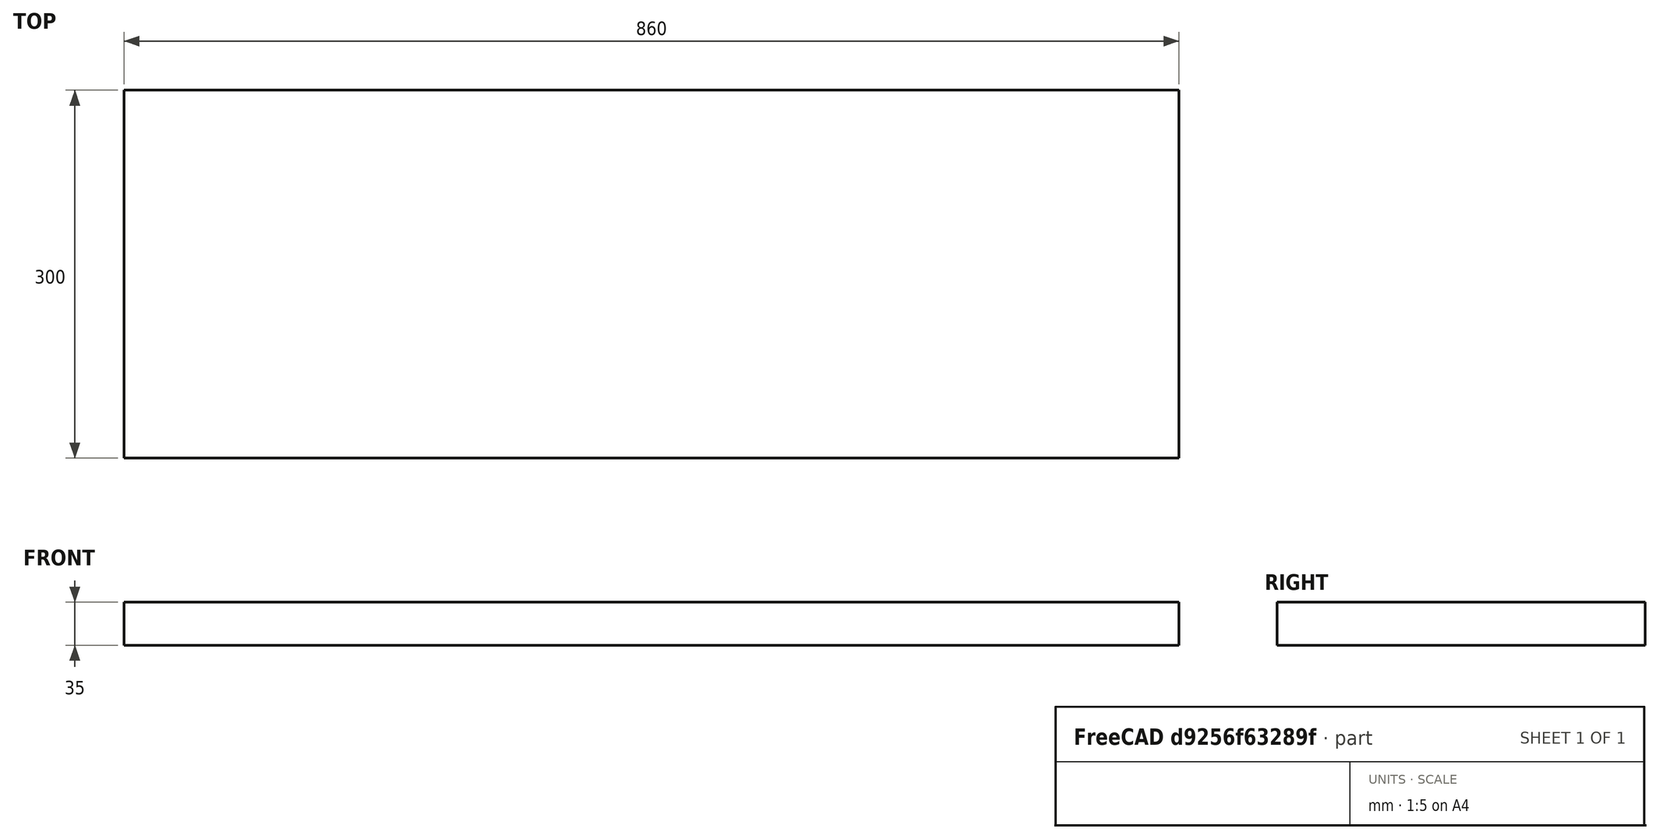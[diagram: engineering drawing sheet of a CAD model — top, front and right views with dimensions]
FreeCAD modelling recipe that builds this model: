
FCSTD DOCUMENT  (FreeCAD 0.18R4 (GitTag))
Label: apron_interior
License: All rights reserved
LicenseURL: http://en.wikipedia.org/wiki/All_rights_reserved
objects: Sketcher::SketchObject×1, PartDesign::Pad×1, PartDesign::Body×1
note: 4 computed .brp shape members not serialized (recipe doc carries the construction recipe); baked Part::Feature solids carry a one-line shape summary decoded from their .brp

FEATURE [Sketcher::SketchObject] Sketch
  MapMode = 5
  Placement = pos=(0,0,0) rot=(0.57735,0.57735,0.57735;2.0944rad)
  Support = -> [YZ_Plane]
  sketch-geometry (4):
    g0: LineSegment StartX=0 StartY=0 StartZ=0 EndX=-300 EndY=0 EndZ=0
    g1: LineSegment StartX=-300 StartY=0 StartZ=0 EndX=-300 EndY=35 EndZ=0
    g2: LineSegment StartX=-300 StartY=35 StartZ=0 EndX=0 EndY=35 EndZ=0
    g3: LineSegment StartX=0 StartY=35 StartZ=0 EndX=0 EndY=0 EndZ=0
  constraints (11):
    c: Coincident(g0,g1)
    c: Coincident(g1,g2)
    c: Coincident(g2,g3)
    c: Coincident(g3,g0)
    c: Horizontal(g0)
    c: Horizontal(g2)
    c: Vertical(g1)
    c: Vertical(g3)
    c: Coincident(g0,g-1)
    c: DistanceY(g3,g3) = 35
    c: DistanceX(g0,g0) = 300
FEATURE [PartDesign::Pad] Pad
  Length = 860
  Length2 = 100
  Placement = pos=(0,0,0) rot=(0.57735,0.57735,0.57735;2.0944rad)
  Profile = -> Sketch
  Type = 0
FEATURE [PartDesign::Body] Body
  Group = -> [Sketch,Pad]
  Origin = -> Origin
  Tip = -> Pad
